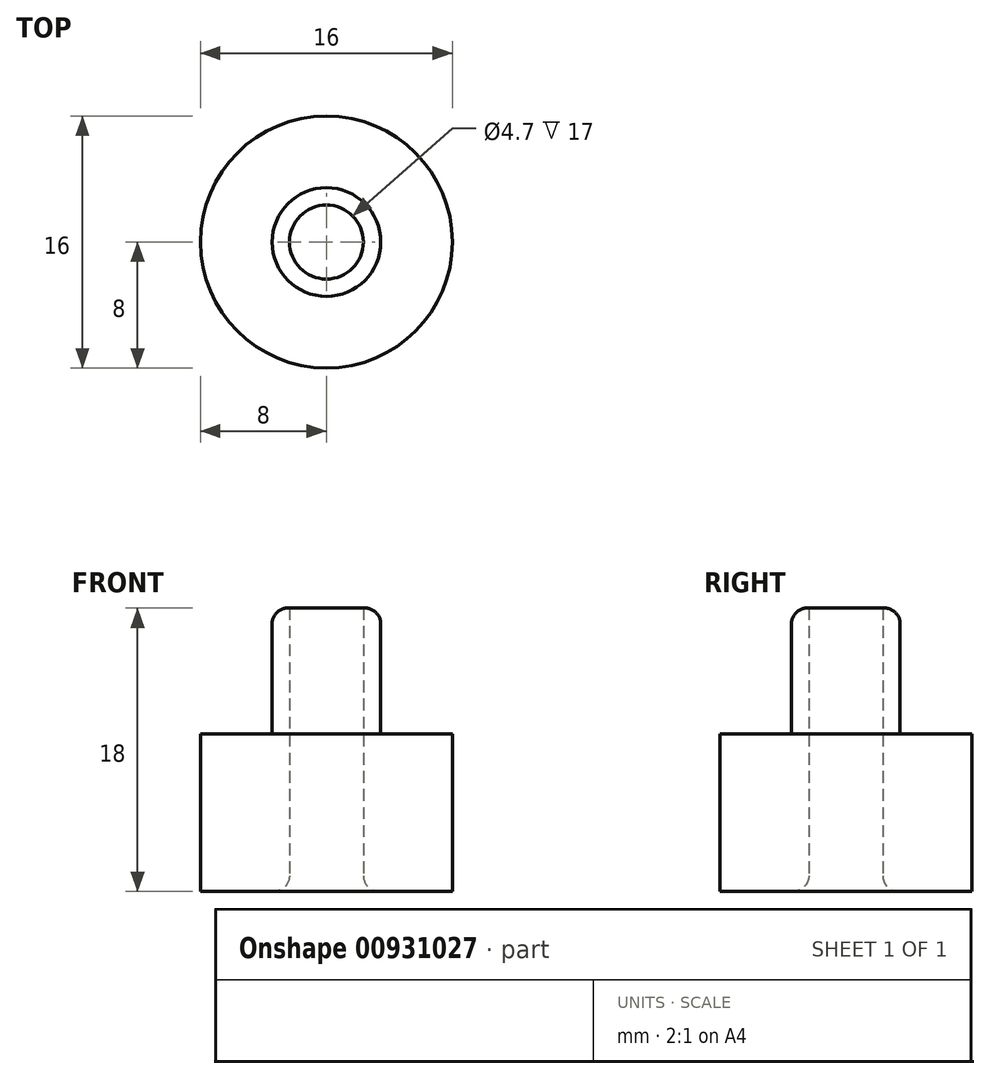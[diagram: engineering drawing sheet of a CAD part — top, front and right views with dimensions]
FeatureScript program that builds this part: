
annotation { "Feature Type Name" : "Feature", "Feature Type Description" : "" }
export const myFeature = defineFeature(function(context is Context, id is Id, definition is map)
    precondition{}
    {
        {
            var Q0;
            Q0=qCreatedBy(makeId("Top.planeOp"),FACE);
            var sketch = newSketch(context, id + "F0", { "sketchPlane" : qUnion([Q0])});
            skCircle(sketch, "E0", {"center": v(0, 0) * mm, "radius": 2.35 * mm});
            skCircle(sketch, "E1", {"center": v(0, 0) * mm, "radius": 3.45 * mm});
            skCircle(sketch, "E2", {"center": v(0, 0) * mm, "radius": 8 * mm});
            skSolve(sketch);
        }
        {
            var Q0;
            Q0=makeQuery(id+"F0.imprint","IMPRINT",FACE,{"disambiguationData":[TD([[makeQuery(id+"F0.imprint","IMPRINT",EDGE,{"derivedFrom":sQuery(id+"F0.wireOp",EDGE,"E0")}),-1.0]])]});
            extrude(context, id + "F1", {"entities" : qUnion([Q0]), "depth" : 18 * mm, "offsetDistance" : 25 * mm});
        }
        {
            var Q0;
            Q0=qCreatedBy(makeId("Top.planeOp"),FACE);
            var sketch = newSketch(context, id + "F2", { "sketchPlane" : qUnion([Q0])});
            skCircle(sketch, "E3", {"center": v(0, 0) * mm, "radius": 8 * mm});
            skCircle(sketch, "E4.0", {"center": v(0, 0) * mm, "radius": 3.45 * mm});
            skSolve(sketch);
        }
        {
            var Q0;
            Q0=makeQuery(id+"F2.imprint","IMPRINT",FACE,{"disambiguationData":[TD([[makeQuery(id+"F2.imprint","IMPRINT",EDGE,{"derivedFrom":sQuery(id+"F2.wireOp",EDGE,"E3")}),1.0]])]});
            extrude(context, id + "F3", {"entities" : qUnion([Q0]), "operationType" : NewBodyOperationType.ADD, "depth" : 10 * mm, "offsetDistance" : 25 * mm});
        }
        {
            var Q0;
            Q0=makeQuery(id+"F1.opExtrude","CAP_EDGE",EDGE,{"disambiguationData":[OSD([sQuery(id+"F0.wireOp",EDGE,"E1")])],"isStart":false});
            fillet(context, id + "F4", {"entities" : qUnion([Q0]), "radius" : 1 * mm, "tangentPropagation" : true, "allowEdgeOverflow" : false});
        }
        {
            var Q0;
            Q0=makeQuery(id+"F1.opExtrude","CAP_EDGE",EDGE,{"disambiguationData":[OSD([sQuery(id+"F0.wireOp",EDGE,"E0")])],"isStart":true});
            fillet(context, id + "F5", {"entities" : qUnion([Q0]), "radius" : 1 * mm, "tangentPropagation" : true, "allowEdgeOverflow" : false});
        }
    });
